# Revit family: BRIDASHD_RCIFM_Extrucol_0009
name_source: partatom
category: Uniones de tubería
units: mm (PartAtom-declared; Revit-internal decimal feet)

## family parameters
Compartido = No
Corte con vacíos al cargar = No
Cota de conector redondo = Diámetro de uso
Número OmniClass = 23.60.30.11.14
Se basa en plano de trabajo = No
Siempre vertical = Sí
Tipo de pieza = Brida
Título OmniClass = Pipework Fittings

## types (1)
- IJ-010P
    Bols Length = 5 29/32"
    Código de montaje = D2090800
    Descripción = SPEARS® EverTUFF® Industrial Schedule 80 CPVC/PVC pipe and fitting designs combine years of proven experience with computer generated stress analysis to yield the optimum physical structure and performance for each fitting. Material reinforcement is uniformly placed in stress concentration areas for substantially improved pressure handling capability. Spears® EverTUFF® CPVC/PVC pipe, fittings and Spears® CPVC/PVC solvent cement are Certified lead-free by NSF®International (NSF®) in accordance with ANSI/NSF® 61 and NSF® 372 for compliance with all State & Federal Regulations. Approved by national, state and most municipal building codes and listed by ICC to ASTM E84 for Flame & Smoke Characteristics of less than 25/50 for use in return air plenums (See PMG Listing No. PMG-1278 at www.icc-es-pmg.org) Resulting products are subjected to numerous verification tests to assure the very best CPVC/PVC piping products available.
    Edition number = 1
    Elevación por defecto = 0"
    Fabricante = Spears Manufacturing
    Lookup Table Name = SCH80 PP Flange Insulating Joint Class150
    Modelo = SCH80 PP Flange Insulating Joint Class150
    Nota clave = 15000
    Product Guid = 91380ae2-f641-499b-b913-b2e2b34643e0
    Product Material = Polypropylene - Spears Manufacturing
    Product data url = https://www.bimobject.com
    URL = https://www.parts.spearsmfg.com

## geometry (parser evidence)
native form markers: Sweep x6
no freeform markers — native parametric forms only
